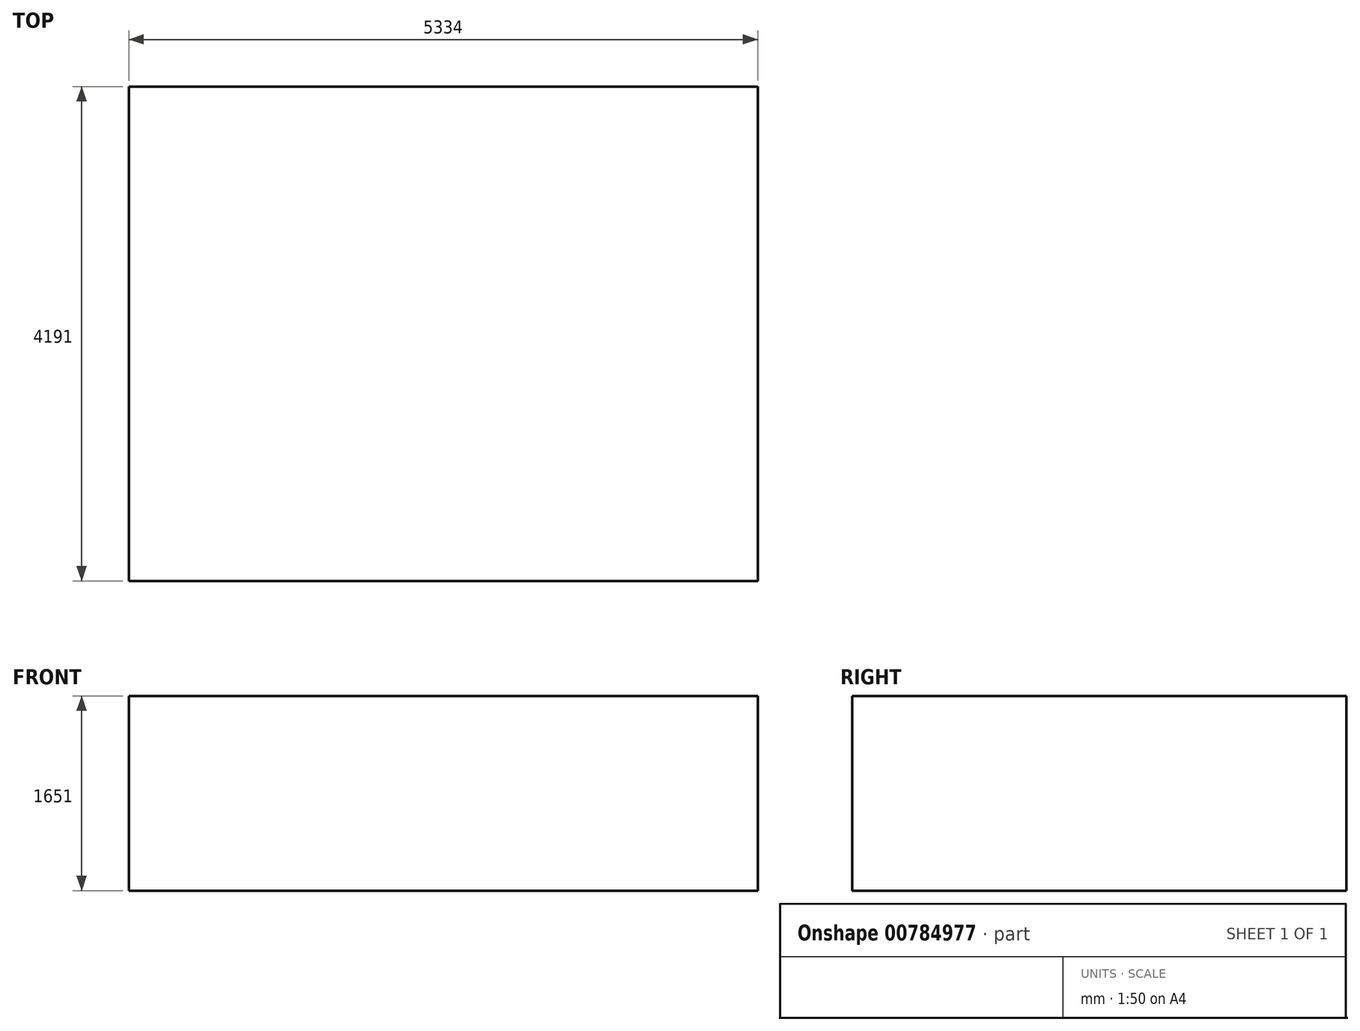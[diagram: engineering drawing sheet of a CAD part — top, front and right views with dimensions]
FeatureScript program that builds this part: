
annotation { "Feature Type Name" : "Feature", "Feature Type Description" : "" }
export const myFeature = defineFeature(function(context is Context, id is Id, definition is map)
    precondition{}
    {
        {
            var Q0;
            Q0=qCreatedBy(makeId("Top.planeOp"),FACE);
            var sketch = newSketch(context, id + "F0", { "sketchPlane" : qUnion([Q0])});
            skLineSegment(sketch, "E0.bottom", {"start": v(0, 0) * mm, "end": v(5334, 0) * mm});
            skLineSegment(sketch, "E0.top", {"start": v(0, 4191) * mm, "end": v(5334, 4191) * mm});
            skLineSegment(sketch, "E0.left", {"start": v(0, 0) * mm, "end": v(0, 4191) * mm});
            skLineSegment(sketch, "E0.right", {"start": v(5334, 0) * mm, "end": v(5334, 4191) * mm});
            skSolve(sketch);
        }
        {
            var Q0;
            Q0=makeQuery(id+"F0.imprint","IMPRINT",FACE,{"disambiguationData":[TD([[makeQuery(id+"F0.imprint","IMPRINT",EDGE,{"derivedFrom":sQuery(id+"F0.wireOp",EDGE,"E0.bottom")}),1.0]])]});
            extrude(context, id + "F1", {"entities" : qUnion([Q0]), "depth" : 1651 * mm, "offsetDistance" : 25.4 * mm});
        }
    });
